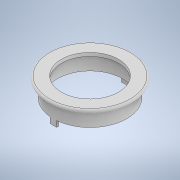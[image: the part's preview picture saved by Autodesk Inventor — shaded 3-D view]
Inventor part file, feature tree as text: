
AUTODESK INVENTOR PART (.ipt)
format: ipt  version: 2022 (Build 260153000, 153)  size: 156,672 bytes
history: native  units: mm
features: extrude x3, sketch x3, fillet x1
ambient origin geometry x8: Origin, YZ Plane, XZ Plane, XY Plane, X Axis, Y Axis, Z Axis, Center Point
bodies: Solid1 (feature_tree)
feature tree (7):
  extrude  "Extrusion1"  Depth=3.5mm
  extrude  "Extrusion2"  Depth=13.25mm
  extrude  "Extrusion3"  Depth=3.0mm TaperAngle=0.0deg
  fillet  "Fillet1"  Radius=2.85mm
  sketch  "Sketch1"  dims[d0=56.0mm d1=3.5mm]
  sketch  "Sketch2"  dims[d2=13.25mm d3=0.0mm d4=3.5mm]
  sketch  "Sketch3"  dims[d5=4.5mm d6=3.0mm d7=0.0mm d8=2.85mm d9=2.85mm d10=5.0mm d11=0.0mm d14=1.5mm]
